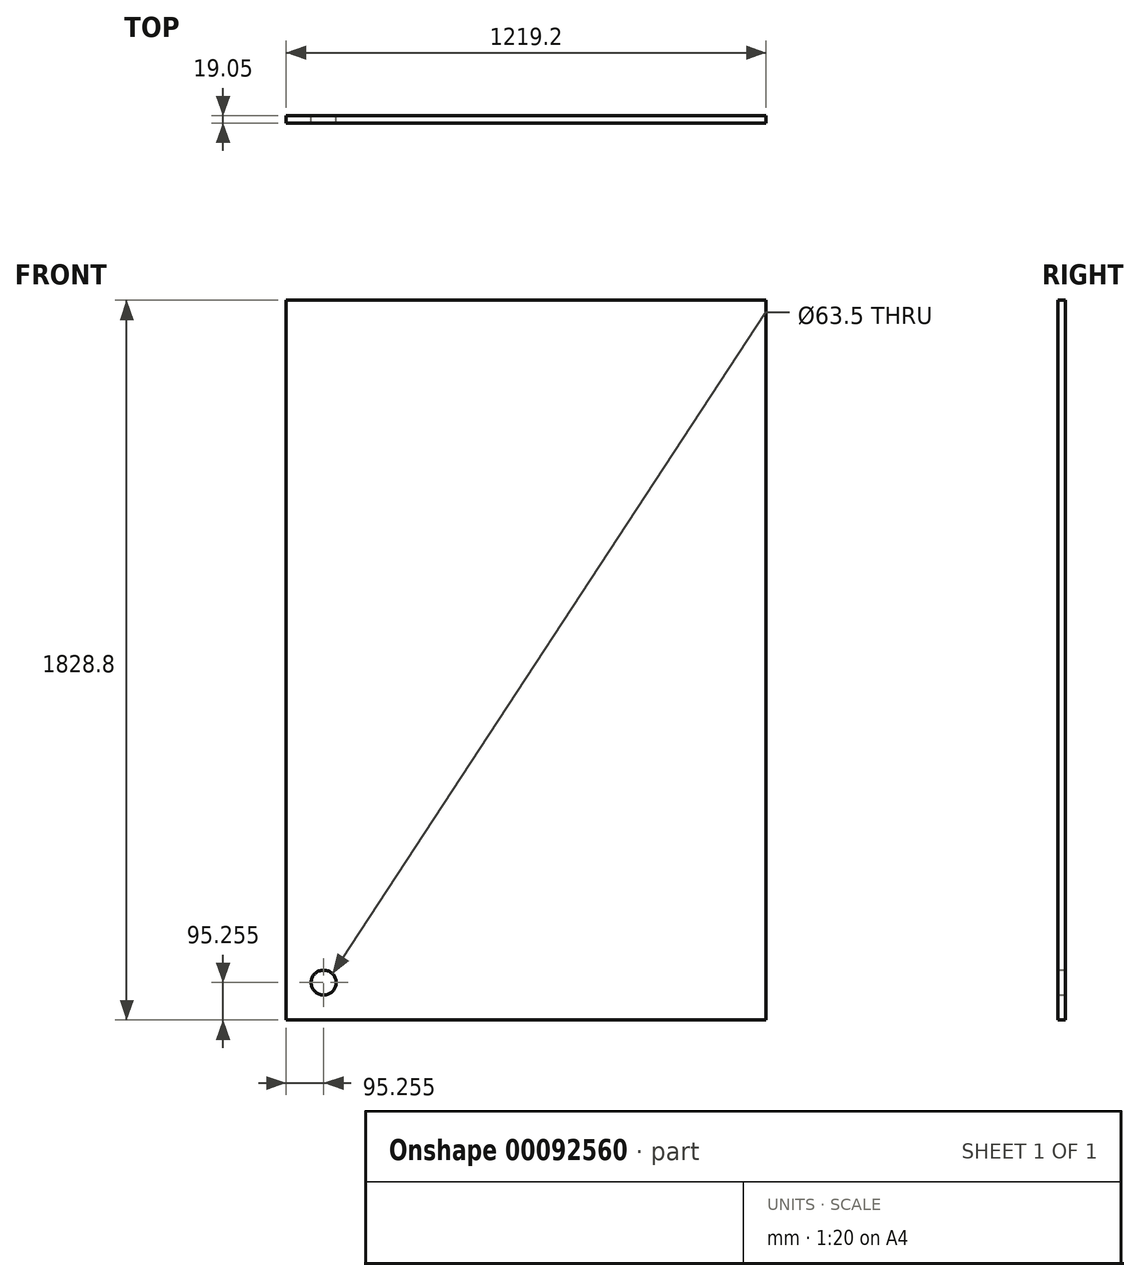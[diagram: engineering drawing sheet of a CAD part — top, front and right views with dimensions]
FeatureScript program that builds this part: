
annotation { "Feature Type Name" : "Feature", "Feature Type Description" : "" }
export const myFeature = defineFeature(function(context is Context, id is Id, definition is map)
    precondition{}
    {
        {
            var Q0;
            Q0=qCreatedBy(makeId("Front.planeOp"),FACE);
            var sketch = newSketch(context, id + "F0", { "sketchPlane" : qUnion([Q0])});
            skLineSegment(sketch, "E0.bottom", {"start": v(-613.47, 1534) * mm, "end": v(605.73, 1534) * mm});
            skLineSegment(sketch, "E0.top", {"start": v(-613.47, -294.8) * mm, "end": v(605.73, -294.8) * mm});
            skLineSegment(sketch, "E0.left", {"start": v(-613.47, 1534) * mm, "end": v(-613.47, -294.8) * mm});
            skLineSegment(sketch, "E0.right", {"start": v(605.73, 1534) * mm, "end": v(605.73, -294.8) * mm});
            skCircle(sketch, "E1", {"center": v(-518.22, -199.56) * mm, "radius": 31.75 * mm});
            skSolve(sketch);
        }
        {
            var Q0;
            Q0=makeQuery(id+"F0.imprint","IMPRINT",FACE,{"disambiguationData":[TD([[makeQuery(id+"F0.imprint","IMPRINT",EDGE,{"derivedFrom":sQuery(id+"F0.wireOp",EDGE,"E0.bottom")}),-1.0]])]});
            extrude(context, id + "F1", {"entities" : qUnion([Q0]), "depth" : 19.05 * mm});
        }
        {
            var Q0;
            Q0=sQuery(id+"F0.wireOp",EDGE,"E1");
            extrude(context, id + "F2", {"bodyType" : ToolBodyType.SURFACE, "surfaceEntities" : qUnion([Q0]), "depth" : 19.05 * mm});
        }
    });
